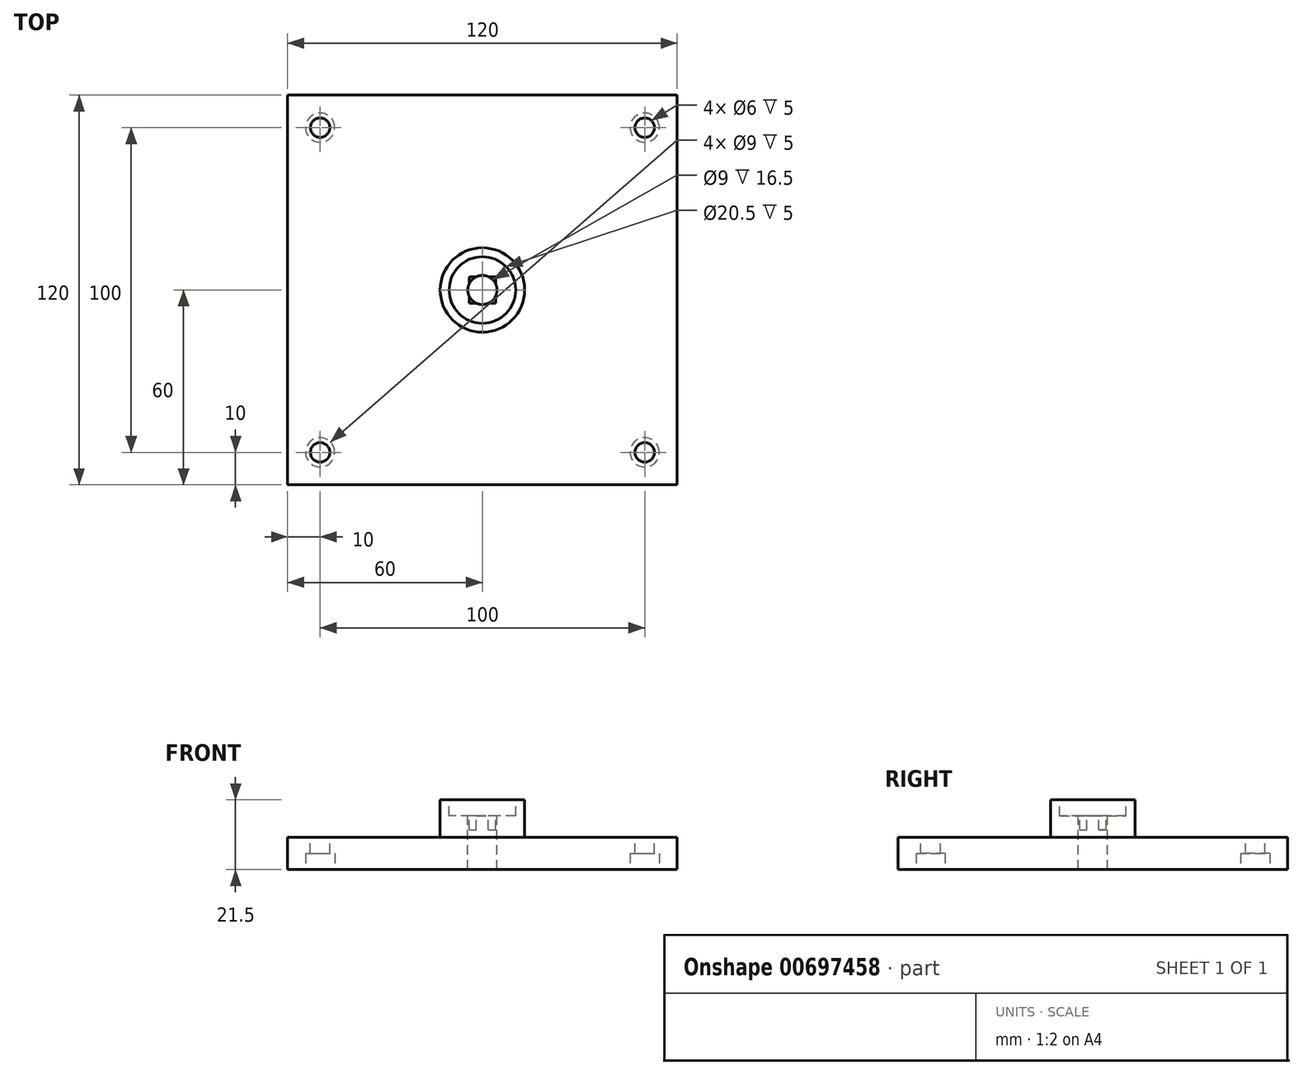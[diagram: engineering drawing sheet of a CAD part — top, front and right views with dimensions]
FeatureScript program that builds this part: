
annotation { "Feature Type Name" : "Feature", "Feature Type Description" : "" }
export const myFeature = defineFeature(function(context is Context, id is Id, definition is map)
    precondition{}
    {
        {
            var Q0;
            Q0=qCreatedBy(makeId("Top.planeOp"),FACE);
            var sketch = newSketch(context, id + "F0", { "sketchPlane" : qUnion([Q0])});
            skLineSegment(sketch, "E0", {"start": v(-111.3, 0) * mm, "end": v(135.5, 0) * mm});
            skLineSegment(sketch, "E1", {"start": v(0, -83.36) * mm, "end": v(0, 82.93) * mm});
            skLineSegment(sketch, "E2.0", {"start": v(-60, 60) * mm, "end": v(60, 60) * mm});
            skLineSegment(sketch, "E3.0", {"start": v(-60, -60) * mm, "end": v(60, -60) * mm});
            skLineSegment(sketch, "E4.0", {"start": v(-60, -60) * mm, "end": v(-60, 60) * mm});
            skLineSegment(sketch, "E5.0", {"start": v(60, -60) * mm, "end": v(60, 60) * mm});
            skSolve(sketch);
        }
        {
            var Q0;
            Q0 = qSketchRegion(id + "F0", true);
            extrude(context, id + "F1", {"entities" : qUnion([Q0]), "depth" : 10 * mm, "offsetDistance" : 25 * mm});
        }
        {
            var Q0;
            Q0=makeQuery(id+"F1.opExtrude","CAP_FACE",FACE,{"disambiguationData":[OSD([sQuery(id+"F0.wireOp",EDGE,"E2.0"),sQuery(id+"F0.wireOp",EDGE,"E3.0"),sQuery(id+"F0.wireOp",EDGE,"E4.0"),sQuery(id+"F0.wireOp",EDGE,"E5.0")])],"isStart":false});
            var sketch = newSketch(context, id + "F2", { "sketchPlane" : qUnion([Q0])});
            skLineSegment(sketch, "E6", {"start": v(0, 0) * mm, "end": v(0, 65.1) * mm});
            skLineSegment(sketch, "E7", {"start": v(0, 0) * mm, "end": v(-77.66, 0) * mm});
            skCircle(sketch, "E8", {"center": v(-50, 50) * mm, "radius": 3 * mm});
            skCircle(sketch, "E9.MirrorC", {"center": v(50, 50) * mm, "radius": 3 * mm});
            skCircle(sketch, "E10.MirrorC", {"center": v(-50, -50) * mm, "radius": 3 * mm});
            skCircle(sketch, "E11.MirrorC", {"center": v(50, -50) * mm, "radius": 3 * mm});
            skSolve(sketch);
        }
        {
            var Q0;
            Q0 = qSketchRegion(id + "F2", true);
            extrude(context, id + "F3", {"entities" : qUnion([Q0]), "operationType" : NewBodyOperationType.REMOVE, "oppositeDirection" : true, "depth" : 25 * mm, "offsetDistance" : 25 * mm});
        }
        {
            var Q0;
            Q0=makeQuery(id+"F1.opExtrude","CAP_FACE",FACE,{"disambiguationData":[OSD([sQuery(id+"F0.wireOp",EDGE,"E2.0"),sQuery(id+"F0.wireOp",EDGE,"E3.0"),sQuery(id+"F0.wireOp",EDGE,"E4.0"),sQuery(id+"F0.wireOp",EDGE,"E5.0")])],"isStart":true});
            var sketch = newSketch(context, id + "F4", { "sketchPlane" : qUnion([Q0])});
            skCircle(sketch, "E12", {"center": v(-50, 50) * mm, "radius": 4.5 * mm});
            skCircle(sketch, "E13", {"center": v(50, 50) * mm, "radius": 4.5 * mm});
            skCircle(sketch, "E14", {"center": v(-50, -50) * mm, "radius": 4.5 * mm});
            skCircle(sketch, "E15", {"center": v(50, -50) * mm, "radius": 4.5 * mm});
            skSolve(sketch);
        }
        {
            var Q0;
            Q0 = qSketchRegion(id + "F4", true);
            extrude(context, id + "F5", {"entities" : qUnion([Q0]), "operationType" : NewBodyOperationType.REMOVE, "oppositeDirection" : true, "depth" : 5 * mm, "offsetDistance" : 25 * mm});
        }
        {
            var Q0;
            Q0=makeQuery(id+"F1.opExtrude","CAP_FACE",FACE,{"disambiguationData":[OSD([sQuery(id+"F0.wireOp",EDGE,"E2.0"),sQuery(id+"F0.wireOp",EDGE,"E3.0"),sQuery(id+"F0.wireOp",EDGE,"E4.0"),sQuery(id+"F0.wireOp",EDGE,"E5.0")])],"isStart":false});
            var sketch = newSketch(context, id + "F6", { "sketchPlane" : qUnion([Q0])});
            skCircle(sketch, "E16", {"center": v(0, 0) * mm, "radius": 13 * mm});
            skSolve(sketch);
        }
        {
            var Q0;
            Q0 = qSketchRegion(id + "F6", true);
            extrude(context, id + "F7", {"entities" : qUnion([Q0]), "operationType" : NewBodyOperationType.ADD, "depth" : 11.5 * mm, "offsetDistance" : 25 * mm});
        }
        {
            var Q0;
            Q0=makeQuery(id+"F7.opExtrude","CAP_FACE",FACE,{"disambiguationData":[OSD([sQuery(id+"F6.wireOp",EDGE,"E16")])],"isStart":false});
            var sketch = newSketch(context, id + "F8", { "sketchPlane" : qUnion([Q0])});
            skCircle(sketch, "E17", {"center": v(0, 0) * mm, "radius": 4.5 * mm});
            skSolve(sketch);
        }
        {
            var Q0;
            Q0 = qSketchRegion(id + "F8", true);
            extrude(context, id + "F9", {"entities" : qUnion([Q0]), "operationType" : NewBodyOperationType.REMOVE, "oppositeDirection" : true, "depth" : 25 * mm, "offsetDistance" : 25 * mm});
        }
        {
            var Q0;
            Q0=makeQuery(id+"F7.opExtrude","CAP_FACE",FACE,{"disambiguationData":[OSD([sQuery(id+"F6.wireOp",EDGE,"E16")])],"isStart":false});
            var sketch = newSketch(context, id + "F10", { "sketchPlane" : qUnion([Q0])});
            skLineSegment(sketch, "E18.bottom", {"start": v(-4.1, -4.1) * mm, "end": v(4.1, -4.1) * mm});
            skLineSegment(sketch, "E18.top", {"start": v(-4.1, 4.1) * mm, "end": v(4.1, 4.1) * mm});
            skLineSegment(sketch, "E18.left", {"start": v(-4.1, -4.1) * mm, "end": v(-4.1, 4.1) * mm});
            skLineSegment(sketch, "E18.right", {"start": v(4.1, -4.1) * mm, "end": v(4.1, 4.1) * mm});
            skSolve(sketch);
        }
        {
            var Q0;
            Q0 = qSketchRegion(id + "F10", true);
            extrude(context, id + "F11", {"entities" : qUnion([Q0]), "operationType" : NewBodyOperationType.REMOVE, "oppositeDirection" : true, "depth" : 9.2 * mm, "offsetDistance" : 25 * mm});
        }
        {
            var Q0;
            Q0=makeQuery(id+"F7.opExtrude","CAP_FACE",FACE,{"disambiguationData":[OSD([sQuery(id+"F6.wireOp",EDGE,"E16")])],"isStart":false});
            var sketch = newSketch(context, id + "F12", { "sketchPlane" : qUnion([Q0])});
            skCircle(sketch, "E19", {"center": v(0, 0) * mm, "radius": 10.25 * mm});
            skSolve(sketch);
        }
        {
            var Q0;
            Q0 = qSketchRegion(id + "F12", true);
            extrude(context, id + "F13", {"entities" : qUnion([Q0]), "operationType" : NewBodyOperationType.REMOVE, "oppositeDirection" : true, "depth" : 5 * mm, "offsetDistance" : 25 * mm});
        }
    });
